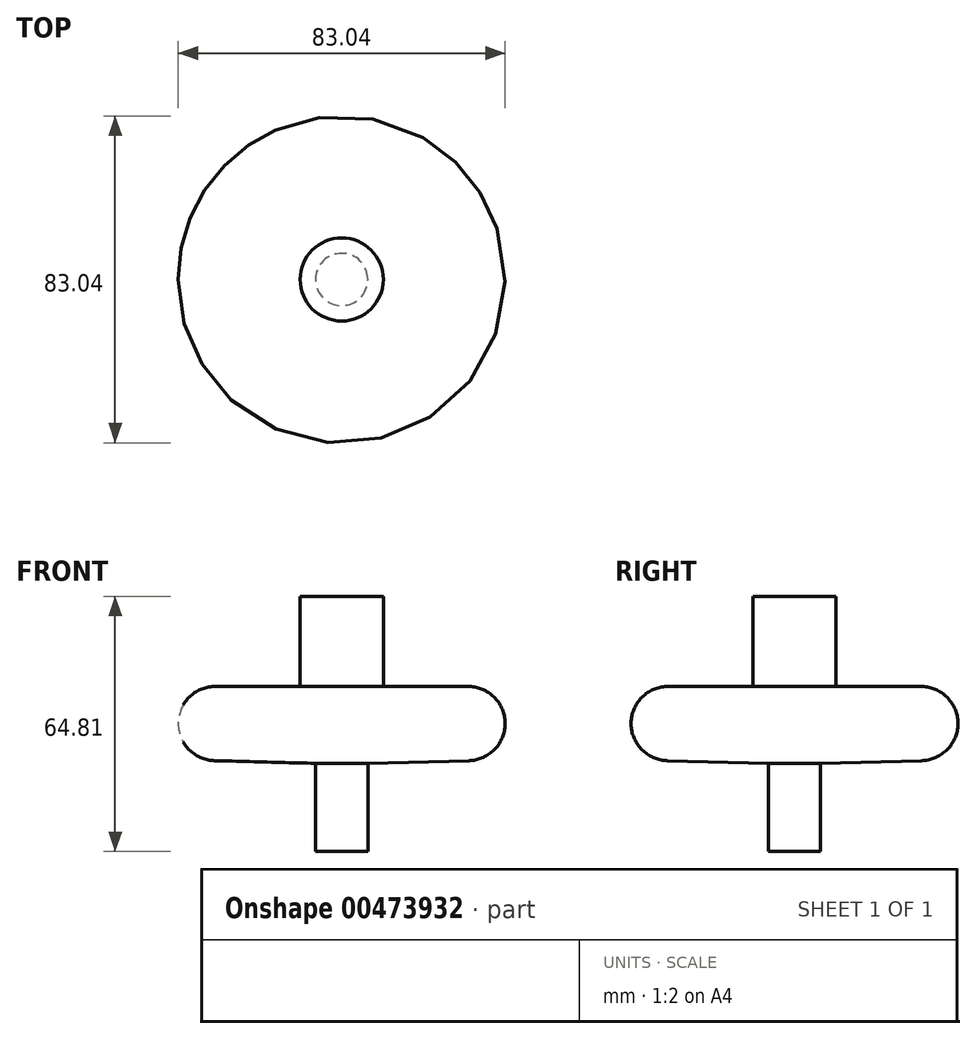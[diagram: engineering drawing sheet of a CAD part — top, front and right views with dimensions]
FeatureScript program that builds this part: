
annotation { "Feature Type Name" : "Feature", "Feature Type Description" : "" }
export const myFeature = defineFeature(function(context is Context, id is Id, definition is map)
    precondition{}
    {
        {
            var Q0;
            Q0=qCreatedBy(makeId("Front.planeOp"),FACE);
            var sketch = newSketch(context, id + "F0", { "sketchPlane" : qUnion([Q0])});
            skLineSegment(sketch, "E0", {"start": v(0, 64.81) * mm, "end": v(10.56, 64.81) * mm});
            skLineSegment(sketch, "E1", {"start": v(10.56, 64.81) * mm, "end": v(10.56, 41.95) * mm});
            skLineSegment(sketch, "E2", {"start": v(10.56, 41.95) * mm, "end": v(32.05, 41.95) * mm});
            skArc(sketch, "E3", {"start": v(32.05, 41.95) * mm, "mid": v(36.78, 40.69) * mm, "end": v(40.25, 37.23) * mm});
            skArc(sketch, "E4", {"start": v(40.25, 37.23) * mm, "mid": v(41.52, 32.5) * mm, "end": v(40.25, 27.79) * mm});
            skArc(sketch, "E5", {"start": v(40.25, 27.79) * mm, "mid": v(36.9, 24.4) * mm, "end": v(32.3, 23.07) * mm});
            skLineSegment(sketch, "E6", {"start": v(0, 0) * mm, "end": v(0, 64.81) * mm});
            skLineSegment(sketch, "E7", {"start": v(32.3, 23.07) * mm, "end": v(6.63, 22.38) * mm});
            skLineSegment(sketch, "E8", {"start": v(6.63, 22.38) * mm, "end": v(6.63, 0) * mm});
            skLineSegment(sketch, "E9", {"start": v(6.63, 0) * mm, "end": v(0, 0) * mm});
            skSolve(sketch);
        }
        {
            var Q0;
            Q0 = qSketchRegion(id + "F0", true);
            var Q1;
            Q1=sQuery(id+"F0.wireOp",EDGE,"E6");
            revolve(context, id + "F1", {"entities" : qUnion([Q0]), "axis" : qUnion([Q1]), "revolveType" : RevolveType.FULL});
        }
    });
